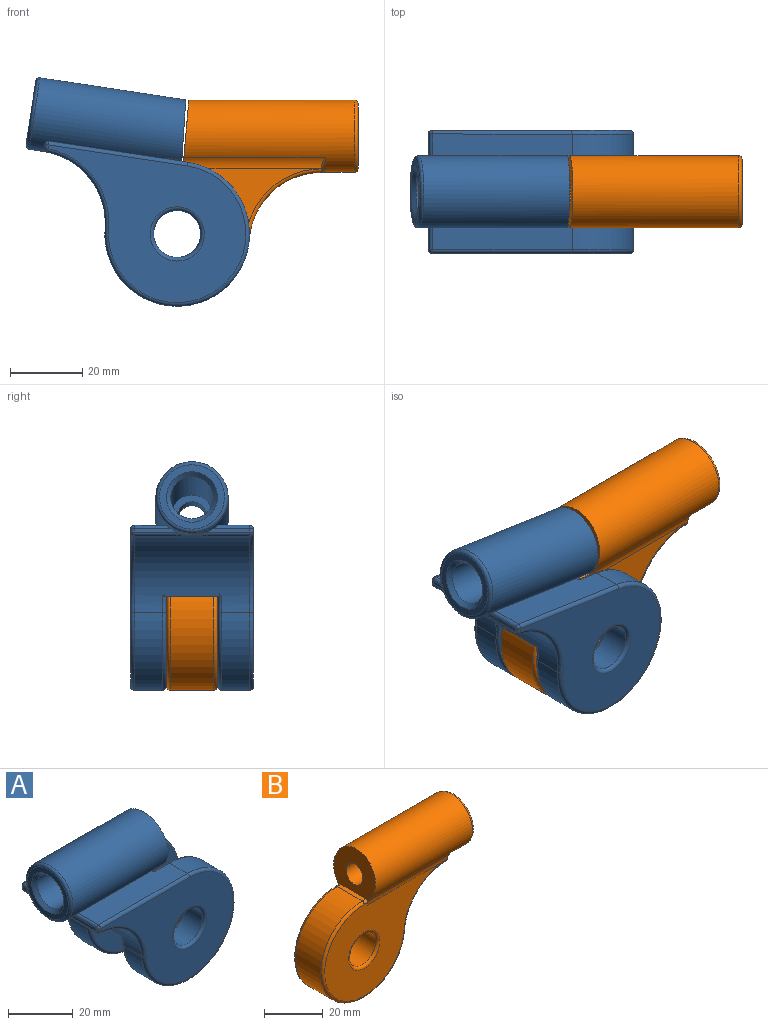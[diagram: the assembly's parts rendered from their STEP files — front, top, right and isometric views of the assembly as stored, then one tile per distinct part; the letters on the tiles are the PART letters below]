
ASSEMBLY  parts=2 mates=1
PART A: 53 faces, bbox 66.8x34.1x59.6 mm
  f0: cylinder r=10mm len=42.22mm, axis (-1,0,0), area 2003.6mm2, adj f2,f4,f9,f12,f17,f20,f21,f22
  f1: cylinder r=4mm len=8mm, axis (-1,0,0), area 192mm2, adj f8,f20
  f2: plane 38.89x8.86mm, normal (0,0,1), area 337.7mm2, adj f0,f3,f17,f28,f38,f49
  f3: cylinder r=20mm len=40mm, axis (0,1,0), area 723.4mm2, adj f2,f10,f29,f39
  f4: plane 38.89x8.86mm, normal (0,0,1), area 337.7mm2, adj f0,f11,f17,f23,f36,f51
  f5: cylinder r=6.5mm len=13mm, axis (0,1,0), area 318.6mm2, adj f32,f33
  f6: plane 18x18mm, normal (-1,0,0), area 98.3mm2, adj f41,f42
  f7: cylinder r=5.85mm len=33.8mm, axis (-1,0,0), area 1242.4mm2, adj f8,f42
  f8: plane 11.7x11.7mm, normal (-1,0,0), area 57.2mm2, adj f1,f7
  f9: plane 11.69x1.02mm, normal (-1,0,0), area 11mm2, adj f0,f25,f44,f51
  f10: cylinder r=20mm len=32mm, axis (0,1,0), area 856.5mm2, adj f3,f11,f17,f26,f31,f35,f40,f43
  f11: cylinder r=20mm len=40mm, axis (0,1,0), area 723.4mm2, adj f4,f10,f24,f37
  f12: plane 11.69x1.02mm, normal (-1,0,0), area 11mm2, adj f0,f30,f47,f49
  f13: cylinder r=6.5mm len=13mm, axis (0,1,0), area 318.6mm2, adj f27,f34
  f14: plane 57.89x38mm, normal (0,-1,0), area 1147.2mm2, adj f23,f24,f25,f26,f27
  f15: plane 57.89x38mm, normal (0,1,0), area 1147.2mm2, adj f28,f29,f30,f31,f32
  f16: plane 39.42x38mm, normal (0,1,0), area 1002.6mm2, adj f17,f34,f35,f36,f37
  f17: cylinder r=21mm len=17.39mm, axis (0,1,0), area 341.1mm2, adj f0,f2,f4,f10,f16,f18,f19,f21
  f18: plane 13.42x4.65mm, normal (0,0,-1), area 62.4mm2, adj f17,f20,f21,f22
  f19: plane 39.42x38mm, normal (0,-1,0), area 1002.6mm2, adj f17,f33,f38,f39,f40
  f20: plane 20.15x17.15mm, normal (1,0,0.09), area 235.2mm2, adj f0,f1,f18,f21,f22
  f21: cylinder r=1mm len=4.65mm, axis (-1,0,0), area 3.4mm2, adj f0,f17,f18,f20
  f22: cylinder r=1mm len=4.65mm, axis (-1,0,0), area 3.4mm2, adj f0,f17,f18,f20
  f23: cylinder r=1mm len=38.89mm, axis (1,0,0), area 61.1mm2, adj f4,f14,f24,f52
  f24: torus R=19mm, axis (0,-1,0), area 143mm2, adj f11,f14,f23,f26
  f25: cylinder r=1mm len=1.02mm, axis (0,0,1), area 1.6mm2, adj f9,f14,f45,f52
  f26: torus R=21mm, axis (0,-1,0), area 46.3mm2, adj f10,f14,f24,f45
  f27: torus R=7.5mm, axis (0,-1,0), area 67.7mm2, adj f13,f14
  f28: cylinder r=1mm len=38.89mm, axis (-1,0,0), area 61.1mm2, adj f2,f15,f29,f50
  f29: torus R=19mm, axis (0,-1,0), area 143mm2, adj f3,f15,f28,f31
  f30: cylinder r=1mm len=1.02mm, axis (0,0,-1), area 1.6mm2, adj f12,f15,f48,f50
  f31: torus R=21mm, axis (0,-1,0), area 46.3mm2, adj f10,f15,f29,f48
  f32: torus R=7.5mm, axis (0,-1,0), area 67.7mm2, adj f5,f15
  f33: torus R=7.5mm, axis (0,-1,0), area 67.7mm2, adj f5,f19
  f34: torus R=7.5mm, axis (0,-1,0), area 67.7mm2, adj f13,f16
  f35: torus R=21mm, axis (0,-1,0), area 8.3mm2, adj f10,f16,f17,f37
  f36: cylinder r=1mm len=8.94mm, axis (-1,0,0), area 11.6mm2, adj f4,f16,f17,f37
  f37: torus R=19mm, axis (0,-1,0), area 143mm2, adj f11,f16,f35,f36
  f38: cylinder r=1mm len=8.94mm, axis (1,0,0), area 11.6mm2, adj f2,f17,f19,f39
  f39: torus R=19mm, axis (0,-1,0), area 143mm2, adj f3,f19,f38,f40
  f40: torus R=21mm, axis (0,-1,0), area 8.3mm2, adj f10,f17,f19,f39
  f41: torus R=9mm, axis (1,0,0), area 95.1mm2, adj f0,f6
  f42: cone r=5.85mm half-angle=45deg, axis (-1,0,0), area 68.8mm2, adj f6,f7
  f43: bspline ~4.49x1.07mm, area 3mm2, adj f0,f10,f44
  f44: cylinder r=1mm len=11.69mm, axis (0,1,0), area 17.8mm2, adj f9,f10,f43,f45
  f45: sphere r=1mm, area 1.5mm2, adj f25,f26,f44
  f46: bspline ~4.49x1.07mm, area 3mm2, adj f0,f10,f47
  f47: cylinder r=1mm len=11.69mm, axis (0,1,0), area 17.8mm2, adj f10,f12,f46,f48
  f48: sphere r=1mm, area 1.5mm2, adj f30,f31,f47
  f49: cylinder r=1mm len=10mm, axis (0,1,0), area 14.5mm2, adj f0,f2,f12,f50
  f50: sphere r=1mm, area 1.6mm2, adj f28,f30,f49
  f51: cylinder r=1mm len=10mm, axis (0,1,0), area 14.5mm2, adj f0,f4,f9,f52
  f52: sphere r=1mm, area 1.6mm2, adj f23,f25,f51
PART B: 30 faces, bbox 71.8x21.8x59.6 mm
  f0: plane 13.8x13.8mm, normal (1,0,0), area 99.3mm2, adj f1,f4
  f1: cylinder r=6.9mm len=39mm, axis (-1,0,0), area 1690.8mm2, adj f0,f27
  f2: plane 18x18mm, normal (1,0,0), area 58.4mm2, adj f26,f27
  f3: cylinder r=10mm len=47.16mm, axis (-1,0,0), area 2205.2mm2, adj f12,f14,f15,f22,f23,f24,f25,f26
  f4: cylinder r=4mm len=8mm, axis (-1,0,0), area 192mm2, adj f0,f12
  f5: plane 2.45x1.54mm, normal (1,0,0), area 1.4mm2, adj f9,f15,f19,f23
  f6: plane 58.89x38mm, normal (0,-1,0), area 1109.9mm2, adj f12,f14,f16,f17,f18,f28
  f7: plane 58.89x38mm, normal (0,1,0), area 1109.9mm2, adj f12,f15,f19,f20,f21,f29
  f8: cylinder r=20mm len=40mm, axis (0,1,0), area 1113mm2, adj f9,f13,f17,f20
  f9: cylinder r=20mm len=19.94mm, axis (0,1,0), area 359mm2, adj f5,f8,f10,f16,f19,f22,f25
  f10: plane 2.45x1.54mm, normal (1,0,0), area 1.4mm2, adj f9,f14,f16,f24
  f11: cylinder r=6.5mm len=13mm, axis (0,1,0), area 490.1mm2, adj f28,f29
  f12: plane 20.15x19.15mm, normal (-1,0,0.09), area 236.4mm2, adj f3,f4,f6,f7,f13,f14,f15,f18
  f13: plane 12x1.75mm, normal (0,0,1), area 21mm2, adj f8,f12,f18,f21
  f14: cylinder r=5mm len=39.31mm, axis (-1,0,0), area 123.9mm2, adj f3,f6,f10,f12,f24
  f15: cylinder r=5mm len=39.31mm, axis (-1,0,0), area 123.9mm2, adj f3,f5,f7,f12,f23
  f16: torus R=21mm, axis (0,-1,0), area 47.8mm2, adj f6,f9,f10,f17
  f17: torus R=19mm, axis (0,-1,0), area 143mm2, adj f6,f8,f16,f18
  f18: cylinder r=1mm len=1.75mm, axis (-1,0,0), area 2.7mm2, adj f6,f12,f13,f17
  f19: torus R=21mm, axis (0,-1,0), area 47.8mm2, adj f5,f7,f9,f20
  f20: torus R=19mm, axis (0,-1,0), area 143mm2, adj f7,f8,f19,f21
  f21: cylinder r=1mm len=1.75mm, axis (1,0,0), area 2.7mm2, adj f7,f12,f13,f20
  f22: bspline ~4.82x1.1mm, area 3.2mm2, adj f3,f9,f23
  f23: torus R=11mm, axis (-1,0,0), area 6.2mm2, adj f3,f5,f15,f22
  f24: torus R=11mm, axis (-1,0,0), area 6.2mm2, adj f3,f10,f14,f25
  f25: bspline ~4.82x1.1mm, area 3.2mm2, adj f3,f9,f24
  f26: torus R=9mm, axis (-1,0,0), area 95.1mm2, adj f2,f3
  f27: torus R=7.9mm, axis (-1,0,0), area 71.7mm2, adj f1,f2
  f28: torus R=7.5mm, axis (0,-1,0), area 67.7mm2, adj f6,f11
  f29: torus R=7.5mm, axis (0,-1,0), area 67.7mm2, adj f7,f11
PLACE A rot(axis=(0,1,0),8.6deg) t=(0,0,0)mm
PLACE B at identity fixed
MATE revolute A.f17 <-> B.f8  axis (0,1,0) through (0,0,0)mm
